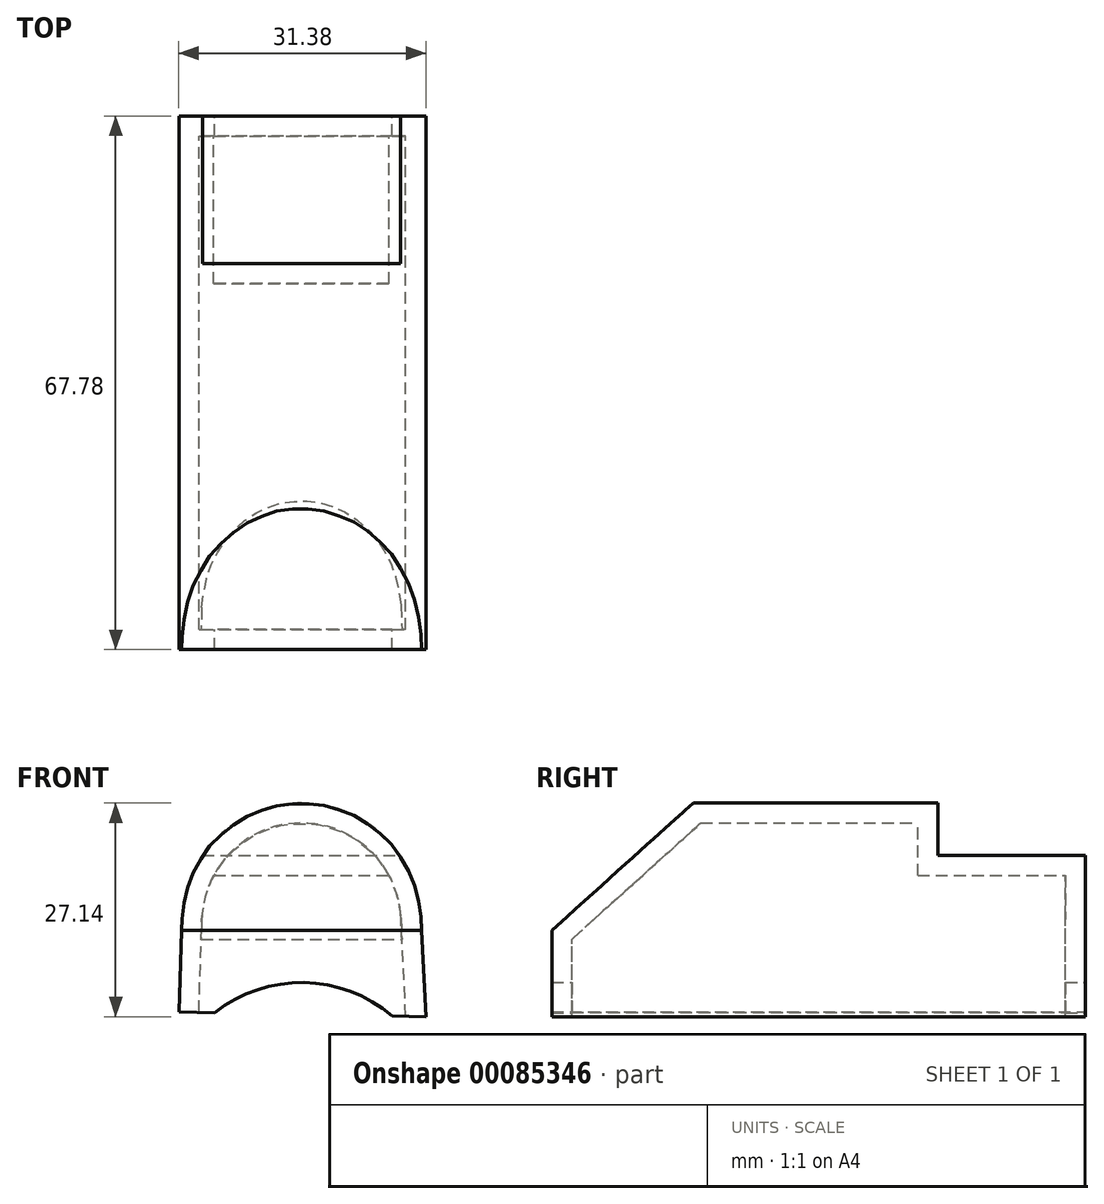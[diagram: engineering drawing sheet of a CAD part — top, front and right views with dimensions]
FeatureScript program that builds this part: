
annotation { "Feature Type Name" : "Feature", "Feature Type Description" : "" }
export const myFeature = defineFeature(function(context is Context, id is Id, definition is map)
    precondition{}
    {
        {
            var Q0;
            Q0=qCreatedBy(makeId("Front.planeOp"),FACE);
            var sketch = newSketch(context, id + "F0", { "sketchPlane" : qUnion([Q0])});
            skArc(sketch, "E0", {"start": v(15.18, 46.94) * mm, "mid": v(-0.14, 61.38) * mm, "end": v(-15.19, 46.67) * mm});
            skLineSegment(sketch, "E1", {"start": v(-15.57, 34.83) * mm, "end": v(-15.19, 46.67) * mm});
            skLineSegment(sketch, "E2", {"start": v(15.8, 34.24) * mm, "end": v(15.18, 46.94) * mm});
            skArc(sketch, "E3", {"start": v(11.53, 34.32) * mm, "mid": v(0.33, 38.56) * mm, "end": v(-11.02, 34.74) * mm});
            skLineSegment(sketch, "E4", {"start": v(-15.57, 34.83) * mm, "end": v(-11.02, 34.74) * mm});
            skLineSegment(sketch, "E5.trimOffspring", {"start": v(11.53, 34.32) * mm, "end": v(15.8, 34.24) * mm});
            skSolve(sketch);
        }
        {
            var Q0;
            Q0 = qSketchRegion(id + "F0", true);
            extrude(context, id + "F1", {"entities" : qUnion([Q0]), "depth" : 67.78 * mm});
        }
        {
            var Q0;
            Q0=qCreatedBy(makeId("Right.planeOp"),FACE);
            var sketch = newSketch(context, id + "F2", { "sketchPlane" : qUnion([Q0])});
            skLineSegment(sketch, "E6", {"start": v(-70.49, 42.78) * mm, "end": v(-47.75, 63.24) * mm});
            skLineSegment(sketch, "E7", {"start": v(-47.75, 63.24) * mm, "end": v(-18.76, 63.24) * mm});
            skLineSegment(sketch, "E8", {"start": v(-18.76, 63.24) * mm, "end": v(-18.76, 54.71) * mm});
            skLineSegment(sketch, "E9", {"start": v(-18.76, 54.71) * mm, "end": v(3.98, 54.71) * mm});
            skLineSegment(sketch, "E10", {"start": v(3.98, 54.71) * mm, "end": v(3.98, 73.19) * mm});
            skLineSegment(sketch, "E11", {"start": v(3.98, 73.19) * mm, "end": v(-71.9, 73.19) * mm});
            skLineSegment(sketch, "E12", {"start": v(-71.9, 73.19) * mm, "end": v(-70.49, 42.78) * mm});
            skSolve(sketch);
        }
        {
            var Q0;
            Q0=makeQuery(id+"F2.imprint","IMPRINT",FACE,{"disambiguationData":[TD([[makeQuery(id+"F2.imprint","IMPRINT",EDGE,{"derivedFrom":sQuery(id+"F2.wireOp",EDGE,"E6")}),1.0]])]});
            extrude(context, id + "F3", {"entities" : qUnion([Q0]), "operationType" : NewBodyOperationType.REMOVE, "endBound" : BoundingType.THROUGH_ALL, "oppositeDirection" : true, "depth" : 28.78 * mm, "hasSecondDirection" : true, "secondDirectionBound" : BoundingType.THROUGH_ALL, "secondDirectionOppositeDirection" : false, "secondDirectionDepth" : 25.4 * mm});
        }
        {
            var Q0;
            Q0=makeQuery(id+"F1.opExtrude","SWEPT_FACE",FACE,{"disambiguationData":[OSD([sQuery(id+"F0.wireOp",EDGE,"E3")])]});
            var Q1;
            Q1=makeQuery(id+"F1.opExtrude","SWEPT_FACE",FACE,{"disambiguationData":[OSD([sQuery(id+"F0.wireOp",EDGE,"E4")])]});
            var Q2;
            Q2=makeQuery(id+"F1.opExtrude","SWEPT_FACE",FACE,{"disambiguationData":[OSD([sQuery(id+"F0.wireOp",EDGE,"E5.trimOffspring")])]});
            shell(context, id + "F4", {"entities" : qUnion([Q0, Q1, Q2]), "thickness" : 2.54 * mm});
        }
    });
